# Revit family: LeL Tago 1.1
name_source: partatom
category: Lighting Fixtures
units: mm (PartAtom-declared; Revit-internal decimal feet)

## family parameters
Cut with Voids When Loaded = Yes
Host = Face
Light Source = No
Part Type = Normal
Room Calculation Point = No
Round Connector Dimension = Use Diameter
Shared = No

## types (7) — shared parameters
Accessories = WCTG11A0T outer casing
Alimentazione = 230 V
Apparent Load = 24 VA
CCT = 3000 K
CRI = 80
Default Elevation = 1219 mm
Description = Outdoor Linear Profile
Finish = LeL Black
IK = IK09
IP = IP65 IP67 IP69
Lamp = LED
Lenght = 520 mm  [stored 1.70604 ft]
Manufacturer = L&L Luce&Light
Model = TG11
Outercasing = 560 mm
Rated Power supply = 230 V
URL = https://www.lucelight.it
Wattage = 24 W
Weight = 2.10 kg

## per-type parameters (varying)
| type | Optic |
| 1.1 A 24W | TAGO Light source : 1.1 A 24W |
| 1.1 G 24W | TAGO Light source : 1.1 G 24W |
| 1.1 K 69° 24W | TAGO Light source : 1.1 K 69° 24W |
| 1.1 L 29° 24W | TAGO Light source : 1.1 L 29° 24W |
| 1.1 M 17° 24W | TAGO Light source : 1.1 M 17° 24W |
| 1.1 S 11° 24W | TAGO Light source : 1.1 S 11° 24W |
| 1.1 W 20°x49° 24W | TAGO Light source : 1.1 W 20°x49° 24W |

note: [stored X ft] marks values corroborated as IEEE doubles in the binary element streams (Revit-internal decimal feet)

## geometry (parser evidence)
native form markers: Sweep x4
no freeform markers — native parametric forms only
